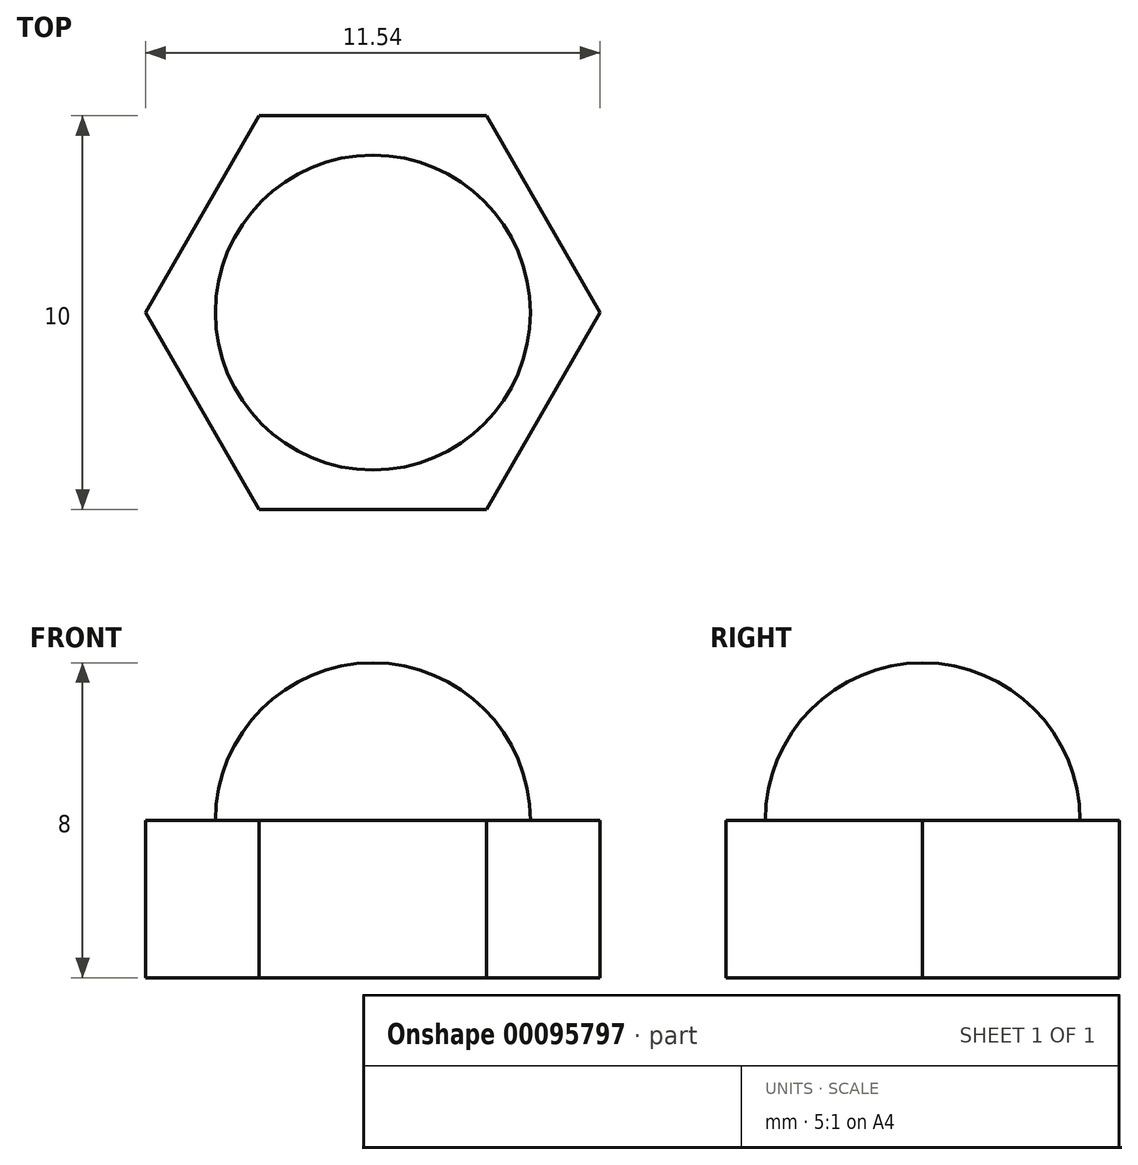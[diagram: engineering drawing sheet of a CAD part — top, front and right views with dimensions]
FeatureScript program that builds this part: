
annotation { "Feature Type Name" : "Feature", "Feature Type Description" : "" }
export const myFeature = defineFeature(function(context is Context, id is Id, definition is map)
    precondition{}
    {
        {
            var Q0;
            Q0=qCreatedBy(makeId("Top.planeOp"),FACE);
            var sketch = newSketch(context, id + "F0", { "sketchPlane" : qUnion([Q0])});
            skCircle(sketch, "E0.cCircle", {"center": v(0, 0) * mm, "radius": 5 * mm, "construction": true});
            skLineSegment(sketch, "E0.0", {"start": v(-2.89, 5) * mm, "end": v(2.89, 5) * mm});
            skLineSegment(sketch, "E0.1", {"start": v(2.89, 5) * mm, "end": v(5.77, 0) * mm});
            skLineSegment(sketch, "E0.2", {"start": v(5.77, 0) * mm, "end": v(2.89, -5) * mm});
            skLineSegment(sketch, "E0.3", {"start": v(2.89, -5) * mm, "end": v(-2.89, -5) * mm});
            skLineSegment(sketch, "E0.4", {"start": v(-2.89, -5) * mm, "end": v(-5.77, 0) * mm});
            skLineSegment(sketch, "E0.5", {"start": v(-5.77, 0) * mm, "end": v(-2.89, 5) * mm});
            skPoint(sketch, "E0.0.midPoint", {"position": v(0, 5) * mm});
            skSolve(sketch);
        }
        {
            var Q0;
            Q0 = qSketchRegion(id + "F0", true);
            extrude(context, id + "F1", {"entities" : qUnion([Q0]), "depth" : 4 * mm});
        }
        {
            var Q0;
            Q0=qCreatedBy(makeId("Front.planeOp"),FACE);
            var sketch = newSketch(context, id + "F2", { "sketchPlane" : qUnion([Q0])});
            skPoint(sketch, "E1", {"position": v(0, 4) * mm});
            skArc(sketch, "E2", {"start": v(4, 4) * mm, "mid": v(0, 8) * mm, "end": v(-4, 4) * mm});
            skLineSegment(sketch, "E3", {"start": v(-4, 4) * mm, "end": v(4, 4) * mm});
            skSolve(sketch);
        }
        {
            var Q0;
            Q0=makeQuery(id+"F2.imprint","IMPRINT",FACE,{"disambiguationData":[TD([[makeQuery(id+"F2.imprint","IMPRINT",EDGE,{"derivedFrom":sQuery(id+"F2.wireOp",EDGE,"E2")}),1.0]])]});
            var Q1;
            Q1=sQuery(id+"F2.wireOp",EDGE,"E3");
            revolve(context, id + "F3", {"operationType" : NewBodyOperationType.ADD, "entities" : qUnion([Q0]), "axis" : qUnion([Q1]), "revolveType" : RevolveType.FULL});
        }
    });
